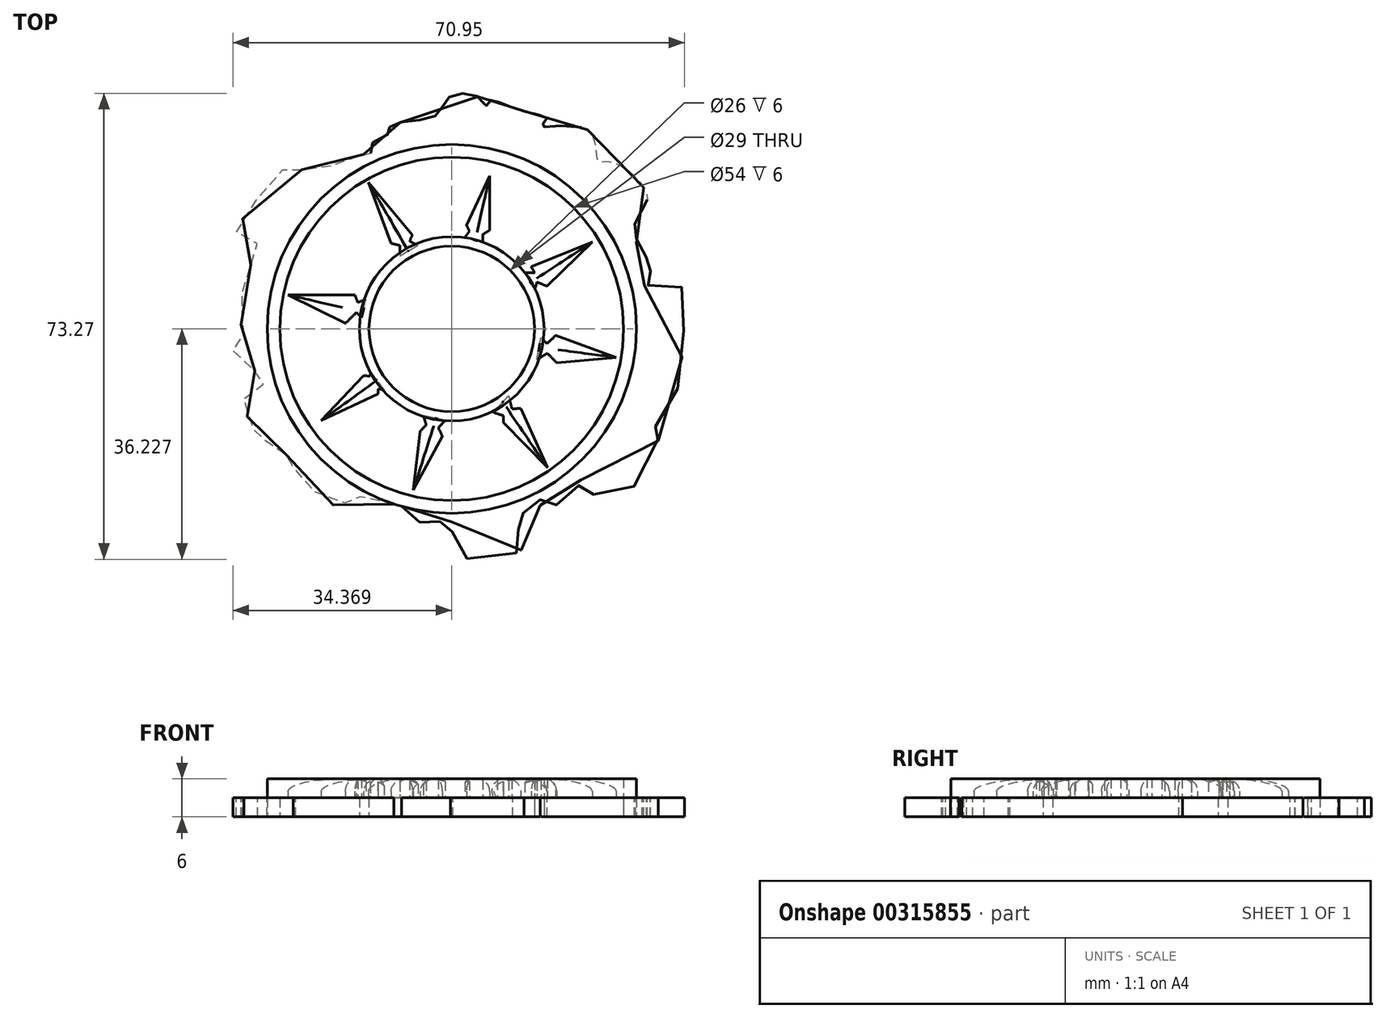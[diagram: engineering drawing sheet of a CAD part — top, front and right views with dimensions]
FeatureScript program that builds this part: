
annotation { "Feature Type Name" : "Feature", "Feature Type Description" : "" }
export const myFeature = defineFeature(function(context is Context, id is Id, definition is map)
    precondition{}
    {
        {
            var Q0;
            Q0=qCreatedBy(makeId("Top.planeOp"),FACE);
            var sketch = newSketch(context, id + "F0", { "sketchPlane" : qUnion([Q0])});
            skCircle(sketch, "E0", {"center": v(-38.6, -30.63) * mm, "radius": 6.5 * mm});
            skCircle(sketch, "E1", {"center": v(-38.6, -30.63) * mm, "radius": 7.25 * mm});
            skCircle(sketch, "E2", {"center": v(-38.6, -30.63) * mm, "radius": 14.5 * mm});
            skCircle(sketch, "E3", {"center": v(-38.6, -30.63) * mm, "radius": 13.5 * mm});
            skCircle(sketch, "E4", {"center": v(-38.6, -30.63) * mm, "radius": 18.94 * mm});
            skSolve(sketch);
        }
        {
            var Q0;
            Q0=makeQuery(id+"F0.imprint","IMPRINT",FACE,{"disambiguationData":[TD([[makeQuery(id+"F0.imprint","IMPRINT",EDGE,{"derivedFrom":sQuery(id+"F0.wireOp",EDGE,"E2")}),-1.0]])]});
            var Q1;
            Q1=makeQuery(id+"F0.imprint","IMPRINT",FACE,{"disambiguationData":[TD([[makeQuery(id+"F0.imprint","IMPRINT",EDGE,{"derivedFrom":sQuery(id+"F0.wireOp",EDGE,"E1")}),-1.0]])]});
            extrude(context, id + "F1", {"entities" : qUnion([Q0, Q1]), "depth" : 1.5 * mm});
        }
        {
            var Q0;
            Q0=makeQuery(id+"F0.imprint","IMPRINT",FACE,{"disambiguationData":[TD([[makeQuery(id+"F0.imprint","IMPRINT",EDGE,{"derivedFrom":sQuery(id+"F0.wireOp",EDGE,"E0")}),1.0]])]});
            extrude(context, id + "F2", {"entities" : qUnion([Q0]), "depth" : 1.5 * mm});
        }
        {
            var Q0;
            Q0=makeQuery(id+"F0.imprint","IMPRINT",FACE,{"disambiguationData":[TD([[makeQuery(id+"F0.imprint","IMPRINT",EDGE,{"derivedFrom":sQuery(id+"F0.wireOp",EDGE,"E0")}),-1.0]])]});
            var Q1;
            Q1=makeQuery(id+"F0.imprint","IMPRINT",FACE,{"disambiguationData":[TD([[makeQuery(id+"F0.imprint","IMPRINT",EDGE,{"derivedFrom":sQuery(id+"F0.wireOp",EDGE,"E2")}),1.0]])]});
            extrude(context, id + "F3", {"entities" : qUnion([Q0, Q1]), "depth" : 3 * mm});
        }
        {
            var Q0;
            Q0=makeQuery(id+"F1.opExtrude","CAP_FACE",FACE,{"disambiguationData":[OSD([sQuery(id+"F0.wireOp",EDGE,"E2"),sQuery(id+"F0.wireOp",EDGE,"E4")])],"isStart":false});
            var sketch = newSketch(context, id + "F4", { "sketchPlane" : qUnion([Q0])});
            skFitSpline(sketch, "E5", {"points": [v(-46.5, -18) * mm, v(-45.94, -16.8) * mm, v(-45.07, -17.04) * mm, v(-44.8, -15.91) * mm, v(-43.72, -15.48) * mm, v(-43.38, -14.66) * mm, v(-39.92, -13.9) * mm, v(-38.76, -12.36) * mm, v(-36.28, -12.56) * mm, v(-35.92, -13.17) * mm, v(-35.64, -12.7) * mm, v(-34.55, -12.95) * mm, v(-31.96, -13.77) * mm, v(-31.1, -14.15) * mm, v(-31.57, -14.7) * mm, v(-27.95, -14.98) * mm, v(-27.15, -17.35) * mm, v(-26, -17.52) * mm, v(-23.25, -20.55) * mm, v(-24.26, -22.27) * mm, v(-23.64, -22.98) * mm, v(-24.16, -23.72) * mm, v(-23.33, -24.67) * mm, v(-23.5, -25.82) * mm, v(-22.98, -26.1) * mm, v(-23.6, -27.16) * mm, v(-21.08, -26.98) * mm, v(-20.36, -29.96) * mm, v(-21.61, -37.2) * mm, v(-23.01, -38.83) * mm, v(-22.4, -39.36) * mm, v(-26.3, -44.26) * mm, v(-28.44, -42.51) * mm, v(-28.92, -43.75) * mm, v(-31.1, -44.35) * mm, v(-31.63, -43.88) * mm, v(-31.87, -45.04) * mm, v(-33.76, -45.11) * mm, v(-32.97, -47.27) * mm, v(-33.6, -48.27) * mm, v(-38.54, -48.12) * mm, v(-38.58, -45.84) * mm, v(-39.53, -45.78) * mm, v(-39.8, -45.55) * mm, v(-41.55, -45.8) * mm, v(-42.55, -44.58) * mm, v(-45.15, -44.23) * mm, v(-46.53, -43.44) * mm, v(-47.2, -44.57) * mm, v(-50.2, -42.7) * mm, v(-51.05, -41.36) * mm, v(-50.92, -40.53) * mm, v(-52.62, -40.53) * mm, v(-53.29, -39.18) * mm, v(-53.89, -38.78) * mm, v(-54.44, -38.06) * mm, v(-54.8, -35.68) * mm, v(-53.46, -35.02) * mm, v(-53.2, -34.17) * mm, v(-54.88, -33.72) * mm, v(-55.7, -31.95) * mm, v(-54.87, -31.2) * mm, v(-55.08, -30.95) * mm, v(-55.07, -29.3) * mm, v(-55.12, -28.68) * mm, v(-55, -27.6) * mm, v(-54.44, -25.78) * mm, v(-54.02, -24.55) * mm, v(-53.95, -23.78) * mm, v(-55.45, -23.13) * mm, v(-54.16, -20.82) * mm, v(-51.76, -18.11) * mm, v(-50.53, -18.47) * mm, v(-50.04, -17.48) * mm, v(-46.5, -18) * mm]});
            skSolve(sketch);
        }
        {
            var Q0;
            {var subQ0=sQuery(id+"F4.wireOp",EDGE,"E5");var subQ1=makeQuery(id+"F1.opExtrude","CAP_EDGE",EDGE,{"disambiguationData":[OSD([sQuery(id+"F0.wireOp",EDGE,"E4")])],"isStart":false});var subQ2=makeQuery(id+"F4.imprint","INTERSECT",VERTEX,{"disambiguationData":[OD(0.0)],"derivedFrom":[subQ1,subQ0]});Q0=makeQuery(id+"F4.imprint","IMPRINT",FACE,{"disambiguationData":[TD([[makeQuery(id+"F4.imprint","IMPRINT",EDGE,{"disambiguationData":[TD([[subQ2,-1.0]])],"derivedFrom":subQ0}),1.0]])]});}
            var Q1;
            {var subQ0=sQuery(id+"F4.wireOp",EDGE,"E5");var subQ1=makeQuery(id+"F1.opExtrude","CAP_EDGE",EDGE,{"disambiguationData":[OSD([sQuery(id+"F0.wireOp",EDGE,"E4")])],"isStart":false});var subQ2=makeQuery(id+"F4.imprint","INTERSECT",VERTEX,{"disambiguationData":[OD(0.0)],"derivedFrom":[subQ1,subQ0]});Q1=makeQuery(id+"F4.imprint","IMPRINT",FACE,{"disambiguationData":[TD([[makeQuery(id+"F4.imprint","IMPRINT",EDGE,{"disambiguationData":[TD([[subQ2,1.0]])],"derivedFrom":subQ0}),1.0]])]});}
            extrude(context, id + "F5", {"entities" : qUnion([Q0, Q1]), "operationType" : NewBodyOperationType.REMOVE, "oppositeDirection" : true, "depth" : 1.5 * mm});
        }
        {
            var Q0;
            {var subQ0=sQuery(id+"F4.wireOp",EDGE,"E5");var subQ1=makeQuery(id+"F1.opExtrude","CAP_EDGE",EDGE,{"disambiguationData":[OSD([sQuery(id+"F0.wireOp",EDGE,"E2")])],"isStart":false});var subQ2=makeQuery(id+"F4.imprint","INTERSECT",VERTEX,{"disambiguationData":[OD(0.0)],"derivedFrom":[subQ1,subQ0]});Q0=makeQuery(id+"F4.imprint","IMPRINT",FACE,{"disambiguationData":[TD([[makeQuery(id+"F4.imprint","IMPRINT",EDGE,{"disambiguationData":[TD([[subQ2,-1.0]])],"derivedFrom":subQ0}),-1.0]])]});}
            var sketch = newSketch(context, id + "F6", { "sketchPlane" : qUnion([Q0])});
            skLineSegment(sketch, "E6", {"start": v(-37.57, -23.46) * mm, "end": v(-37.22, -22.96) * mm});
            skLineSegment(sketch, "E7", {"start": v(-37.22, -22.96) * mm, "end": v(-37.45, -22.46) * mm});
            skLineSegment(sketch, "E8", {"start": v(-37.45, -22.46) * mm, "end": v(-35.62, -18.6) * mm});
            skLineSegment(sketch, "E9", {"start": v(-35.62, -18.6) * mm, "end": v(-35.62, -22.88) * mm});
            skLineSegment(sketch, "E10", {"start": v(-35.62, -22.88) * mm, "end": v(-36.17, -23.2) * mm});
            skLineSegment(sketch, "E11", {"start": v(-36.17, -23.2) * mm, "end": v(-36.17, -23.8) * mm});
            skLineSegment(sketch, "E12", {"start": v(-36.17, -23.8) * mm, "end": v(-37.57, -23.46) * mm});
            skLineSegment(sketch, "E13", {"start": v(-36.87, -23.63) * mm, "end": v(-35.62, -18.6) * mm});
            skLineSegment(sketch, "E14", {"start": v(-35.62, -22.88) * mm, "end": v(-35.9, -23.04) * mm});
            skLineSegment(sketch, "E15", {"start": v(-32.86, -26.23) * mm, "end": v(-32.07, -26.23) * mm});
            skLineSegment(sketch, "E16", {"start": v(-32.07, -26.23) * mm, "end": v(-32.36, -25.76) * mm});
            skLineSegment(sketch, "E17", {"start": v(-32.36, -25.76) * mm, "end": v(-27.56, -23.8) * mm});
            skLineSegment(sketch, "E18", {"start": v(-27.56, -23.8) * mm, "end": v(-31.13, -27.27) * mm});
            skLineSegment(sketch, "E19", {"start": v(-31.13, -27.27) * mm, "end": v(-31.91, -26.96) * mm});
            skLineSegment(sketch, "E20", {"start": v(-31.91, -26.96) * mm, "end": v(-32.07, -27.52) * mm});
            skLineSegment(sketch, "E21", {"start": v(-32.07, -27.52) * mm, "end": v(-32.86, -26.23) * mm});
            skLineSegment(sketch, "E22", {"start": v(-32.47, -26.88) * mm, "end": v(-27.56, -23.8) * mm});
            skLineSegment(sketch, "E23", {"start": v(-31.6, -31.31) * mm, "end": v(-31.12, -31.8) * mm});
            skLineSegment(sketch, "E24", {"start": v(-31.12, -31.8) * mm, "end": v(-30.44, -31.14) * mm});
            skLineSegment(sketch, "E25", {"start": v(-30.44, -31.14) * mm, "end": v(-25.68, -32.88) * mm});
            skLineSegment(sketch, "E26", {"start": v(-25.68, -32.88) * mm, "end": v(-30.36, -33.3) * mm});
            skLineSegment(sketch, "E27", {"start": v(-30.36, -33.3) * mm, "end": v(-31.09, -32.55) * mm});
            skLineSegment(sketch, "E28", {"start": v(-31.09, -32.55) * mm, "end": v(-31.91, -33.05) * mm});
            skLineSegment(sketch, "E29", {"start": v(-31.91, -33.05) * mm, "end": v(-31.6, -31.31) * mm});
            skLineSegment(sketch, "E30", {"start": v(-31.75, -32.18) * mm, "end": v(-25.68, -32.88) * mm});
            skLineSegment(sketch, "E31", {"start": v(-33.19, -36.87) * mm, "end": v(-31.09, -41.53) * mm});
            skLineSegment(sketch, "E32", {"start": v(-31.09, -41.53) * mm, "end": v(-34.53, -38) * mm});
            skLineSegment(sketch, "E33", {"start": v(-35, -36.82) * mm, "end": v(-34.13, -35.89) * mm});
            skLineSegment(sketch, "E34", {"start": v(-34.13, -35.89) * mm, "end": v(-33.87, -36.93) * mm});
            skLineSegment(sketch, "E35", {"start": v(-33.87, -36.93) * mm, "end": v(-33.19, -36.87) * mm});
            skLineSegment(sketch, "E36", {"start": v(-40.83, -37.47) * mm, "end": v(-40.6, -38.17) * mm});
            skLineSegment(sketch, "E37", {"start": v(-40.6, -38.17) * mm, "end": v(-41.07, -38.68) * mm});
            skLineSegment(sketch, "E38", {"start": v(-41.07, -38.68) * mm, "end": v(-41.62, -43.3) * mm});
            skLineSegment(sketch, "E39", {"start": v(-41.62, -43.3) * mm, "end": v(-39.33, -39.09) * mm});
            skLineSegment(sketch, "E40", {"start": v(-39.33, -39.09) * mm, "end": v(-39.66, -38.4) * mm});
            skLineSegment(sketch, "E41", {"start": v(-39.66, -38.4) * mm, "end": v(-39.11, -37.83) * mm});
            skLineSegment(sketch, "E42", {"start": v(-39.11, -37.83) * mm, "end": v(-40.83, -37.47) * mm});
            skLineSegment(sketch, "E43", {"start": v(-39.97, -37.65) * mm, "end": v(-41.62, -43.3) * mm});
            skLineSegment(sketch, "E44", {"start": v(-44.97, -34) * mm, "end": v(-45.02, -34.36) * mm});
            skLineSegment(sketch, "E45", {"start": v(-45.02, -34.36) * mm, "end": v(-45.53, -34.3) * mm});
            skLineSegment(sketch, "E46", {"start": v(-45.53, -34.3) * mm, "end": v(-48.85, -37.83) * mm});
            skLineSegment(sketch, "E47", {"start": v(-48.85, -37.83) * mm, "end": v(-44.4, -35.75) * mm});
            skLineSegment(sketch, "E48", {"start": v(-44.4, -35.75) * mm, "end": v(-44.4, -35.35) * mm});
            skLineSegment(sketch, "E49", {"start": v(-44.4, -35.35) * mm, "end": v(-43.92, -35.4) * mm});
            skLineSegment(sketch, "E50", {"start": v(-43.92, -35.4) * mm, "end": v(-44.97, -34) * mm});
            skLineSegment(sketch, "E51", {"start": v(-44.44, -34.7) * mm, "end": v(-48.85, -37.83) * mm});
            skLineSegment(sketch, "E52", {"start": v(-45.35, -28.32) * mm, "end": v(-45.99, -28.56) * mm});
            skLineSegment(sketch, "E53", {"start": v(-45.99, -28.56) * mm, "end": v(-46.21, -27.96) * mm});
            skLineSegment(sketch, "E54", {"start": v(-46.21, -27.96) * mm, "end": v(-51.45, -27.96) * mm});
            skLineSegment(sketch, "E55", {"start": v(-51.45, -27.96) * mm, "end": v(-46.95, -30.2) * mm});
            skLineSegment(sketch, "E56", {"start": v(-46.95, -30.2) * mm, "end": v(-46.09, -29.33) * mm});
            skLineSegment(sketch, "E57", {"start": v(-46.09, -29.33) * mm, "end": v(-45.68, -29.74) * mm});
            skLineSegment(sketch, "E58", {"start": v(-45.68, -29.74) * mm, "end": v(-45.35, -28.32) * mm});
            skLineSegment(sketch, "E59", {"start": v(-45.52, -29.03) * mm, "end": v(-51.45, -27.96) * mm});
            skLineSegment(sketch, "E60", {"start": v(-41.26, -24.07) * mm, "end": v(-41.91, -23.74) * mm});
            skLineSegment(sketch, "E61", {"start": v(-41.91, -23.74) * mm, "end": v(-41.7, -23.25) * mm});
            skLineSegment(sketch, "E62", {"start": v(-41.7, -23.25) * mm, "end": v(-45.13, -19.12) * mm});
            skLineSegment(sketch, "E63", {"start": v(-45.13, -19.12) * mm, "end": v(-43.36, -23.9) * mm});
            skLineSegment(sketch, "E64", {"start": v(-43.36, -23.9) * mm, "end": v(-42.68, -24.07) * mm});
            skLineSegment(sketch, "E65", {"start": v(-42.68, -24.07) * mm, "end": v(-42.68, -24.9) * mm});
            skLineSegment(sketch, "E66", {"start": v(-42.68, -24.9) * mm, "end": v(-41.26, -24.07) * mm});
            skLineSegment(sketch, "E67", {"start": v(-41.97, -24.48) * mm, "end": v(-45.13, -19.12) * mm});
            skLineSegment(sketch, "E68", {"start": v(-34.53, -38) * mm, "end": v(-34.53, -37.45) * mm});
            skLineSegment(sketch, "E69", {"start": v(-34.53, -37.45) * mm, "end": v(-35.54, -37.13) * mm});
            skLineSegment(sketch, "E70", {"start": v(-35.54, -37.13) * mm, "end": v(-35, -36.82) * mm});
            skLineSegment(sketch, "E71", {"start": v(-31.09, -41.53) * mm, "end": v(-34.72, -36.52) * mm});
            skSolve(sketch);
        }
        {
            var Q0;
            Q0=makeQuery(id+"F6.imprint","IMPRINT",FACE,{"disambiguationData":[TD([[makeQuery(id+"F6.imprint","IMPRINT",EDGE,{"derivedFrom":sQuery(id+"F6.wireOp",EDGE,"E9")}),-1.0]])]});
            var Q1;
            {var subQ1=sQuery(id+"F6.wireOp",EDGE,"E6");Q1=makeQuery(id+"F6.imprint","IMPRINT",FACE,{"disambiguationData":[TD([[makeQuery(id+"F6.imprint","IMPRINT",EDGE,{"derivedFrom":subQ1}),-1.0]])]});}
            extrude(context, id + "F7", {"entities" : qUnion([Q0, Q1]), "depth" : 1.5 * mm});
        }
        {
            var Q0;
            Q0=makeQuery(id+"F7.opExtrude","CAP_EDGE",EDGE,{"disambiguationData":[OSD([sQuery(id+"F6.wireOp",EDGE,"E9")])],"isStart":false});
            var Q1;
            Q1=makeQuery(id+"F7.opExtrude","CAP_EDGE",EDGE,{"disambiguationData":[OSD([sQuery(id+"F6.wireOp",EDGE,"E8")])],"isStart":false});
            fillet(context, id + "F8", {"entities" : qUnion([Q0, Q1]), "radius" : 1 * mm, "tangentPropagation" : true, "allowEdgeOverflow" : false});
        }
        {
            var Q0;
            Q0 = qSketchRegion(id + "F6", true);
            extrude(context, id + "F9", {"entities" : qUnion([Q0]), "depth" : 1.5 * mm});
        }
        {
            var Q0;
            Q0=makeQuery(id+"F9.opExtrude","CAP_EDGE",EDGE,{"disambiguationData":[OSD([sQuery(id+"F6.wireOp",EDGE,"E62")])],"isStart":false});
            var Q1;
            Q1=makeQuery(id+"F9.opExtrude","CAP_EDGE",EDGE,{"disambiguationData":[OSD([sQuery(id+"F6.wireOp",EDGE,"E63")])],"isStart":false});
            var Q2;
            Q2=makeQuery(id+"F9.opExtrude","CAP_EDGE",EDGE,{"disambiguationData":[OSD([sQuery(id+"F6.wireOp",EDGE,"E9")])],"isStart":false});
            var Q3;
            Q3=makeQuery(id+"F9.opExtrude","CAP_EDGE",EDGE,{"disambiguationData":[OSD([sQuery(id+"F6.wireOp",EDGE,"E8")])],"isStart":false});
            var Q4;
            Q4=makeQuery(id+"F9.opExtrude","CAP_EDGE",EDGE,{"disambiguationData":[OSD([sQuery(id+"F6.wireOp",EDGE,"E17")])],"isStart":false});
            var Q5;
            Q5=makeQuery(id+"F9.opExtrude","CAP_EDGE",EDGE,{"disambiguationData":[OSD([sQuery(id+"F6.wireOp",EDGE,"E18")])],"isStart":false});
            var Q6;
            Q6=makeQuery(id+"F9.opExtrude","CAP_EDGE",EDGE,{"disambiguationData":[OSD([sQuery(id+"F6.wireOp",EDGE,"E54")])],"isStart":false});
            var Q7;
            Q7=makeQuery(id+"F9.opExtrude","CAP_EDGE",EDGE,{"disambiguationData":[OSD([sQuery(id+"F6.wireOp",EDGE,"E55")])],"isStart":false});
            var Q8;
            Q8=makeQuery(id+"F9.opExtrude","CAP_EDGE",EDGE,{"disambiguationData":[OSD([sQuery(id+"F6.wireOp",EDGE,"E46")])],"isStart":false});
            var Q9;
            Q9=makeQuery(id+"F9.opExtrude","CAP_EDGE",EDGE,{"disambiguationData":[OSD([sQuery(id+"F6.wireOp",EDGE,"E47")])],"isStart":false});
            var Q10;
            Q10=makeQuery(id+"F9.opExtrude","CAP_EDGE",EDGE,{"disambiguationData":[OSD([sQuery(id+"F6.wireOp",EDGE,"E38")])],"isStart":false});
            var Q11;
            Q11=makeQuery(id+"F9.opExtrude","CAP_EDGE",EDGE,{"disambiguationData":[OSD([sQuery(id+"F6.wireOp",EDGE,"E39")])],"isStart":false});
            var Q12;
            Q12=makeQuery(id+"F9.opExtrude","CAP_EDGE",EDGE,{"disambiguationData":[OSD([sQuery(id+"F6.wireOp",EDGE,"E32")])],"isStart":false});
            var Q13;
            Q13=makeQuery(id+"F9.opExtrude","CAP_EDGE",EDGE,{"disambiguationData":[OSD([sQuery(id+"F6.wireOp",EDGE,"E31")])],"isStart":false});
            var Q14;
            Q14=makeQuery(id+"F9.opExtrude","CAP_EDGE",EDGE,{"disambiguationData":[OSD([sQuery(id+"F6.wireOp",EDGE,"E26")])],"isStart":false});
            var Q15;
            Q15=makeQuery(id+"F9.opExtrude","CAP_EDGE",EDGE,{"disambiguationData":[OSD([sQuery(id+"F6.wireOp",EDGE,"E25")])],"isStart":false});
            fillet(context, id + "F10", {"entities" : qUnion([Q0, Q1, Q2, Q3, Q4, Q5, Q6, Q7, Q8, Q9, Q10, Q11, Q12, Q13, Q14, Q15]), "radius" : 1 * mm, "tangentPropagation" : true, "allowEdgeOverflow" : false});
        }
        {
            var Q0;
            Q0=makeQuery(id+"F9.opExtrude","SWEPT_BODY",BODY,{"disambiguationData":[OSD([sQuery(id+"F6.wireOp",EDGE,"E60"),sQuery(id+"F6.wireOp",EDGE,"E61"),sQuery(id+"F6.wireOp",EDGE,"E62"),sQuery(id+"F6.wireOp",EDGE,"E63"),sQuery(id+"F6.wireOp",EDGE,"E64"),sQuery(id+"F6.wireOp",EDGE,"E65"),sQuery(id+"F6.wireOp",EDGE,"E66")])]});
            var Q1;
            Q1=makeQuery(id+"F9.opExtrude","SWEPT_BODY",BODY,{"disambiguationData":[OSD([sQuery(id+"F6.wireOp",EDGE,"E52"),sQuery(id+"F6.wireOp",EDGE,"E53"),sQuery(id+"F6.wireOp",EDGE,"E54"),sQuery(id+"F6.wireOp",EDGE,"E55"),sQuery(id+"F6.wireOp",EDGE,"E56"),sQuery(id+"F6.wireOp",EDGE,"E57"),sQuery(id+"F6.wireOp",EDGE,"E58")])]});
            var Q2;
            Q2=makeQuery(id+"F9.opExtrude","SWEPT_BODY",BODY,{"disambiguationData":[OSD([sQuery(id+"F6.wireOp",EDGE,"E36"),sQuery(id+"F6.wireOp",EDGE,"E37"),sQuery(id+"F6.wireOp",EDGE,"E38"),sQuery(id+"F6.wireOp",EDGE,"E39"),sQuery(id+"F6.wireOp",EDGE,"E40"),sQuery(id+"F6.wireOp",EDGE,"E41"),sQuery(id+"F6.wireOp",EDGE,"E42")])]});
            var Q3;
            Q3=makeQuery(id+"F9.opExtrude","SWEPT_BODY",BODY,{"disambiguationData":[OSD([sQuery(id+"F6.wireOp",EDGE,"E44"),sQuery(id+"F6.wireOp",EDGE,"E45"),sQuery(id+"F6.wireOp",EDGE,"E46"),sQuery(id+"F6.wireOp",EDGE,"E47"),sQuery(id+"F6.wireOp",EDGE,"E48"),sQuery(id+"F6.wireOp",EDGE,"E49"),sQuery(id+"F6.wireOp",EDGE,"E50")])]});
            var Q4;
            Q4=makeQuery(id+"F9.opExtrude","SWEPT_BODY",BODY,{"disambiguationData":[OSD([sQuery(id+"F6.wireOp",EDGE,"E15"),sQuery(id+"F6.wireOp",EDGE,"E16"),sQuery(id+"F6.wireOp",EDGE,"E17"),sQuery(id+"F6.wireOp",EDGE,"E18"),sQuery(id+"F6.wireOp",EDGE,"E19"),sQuery(id+"F6.wireOp",EDGE,"E20"),sQuery(id+"F6.wireOp",EDGE,"E21")])]});
            var Q5;
            Q5=makeQuery(id+"F9.opExtrude","SWEPT_BODY",BODY,{"disambiguationData":[OSD([sQuery(id+"F6.wireOp",EDGE,"E6"),sQuery(id+"F6.wireOp",EDGE,"E7"),sQuery(id+"F6.wireOp",EDGE,"E8"),sQuery(id+"F6.wireOp",EDGE,"E9"),sQuery(id+"F6.wireOp",EDGE,"E10"),sQuery(id+"F6.wireOp",EDGE,"E11"),sQuery(id+"F6.wireOp",EDGE,"E12"),sQuery(id+"F6.wireOp",EDGE,"E14")])]});
            var Q6;
            Q6=makeQuery(id+"F2.opExtrude","SWEPT_BODY",BODY,{"disambiguationData":[OSD([sQuery(id+"F0.wireOp",EDGE,"E0")])]});
            var Q7;
            Q7=makeQuery(id+"F3.opExtrude","SWEPT_BODY",BODY,{"disambiguationData":[OSD([sQuery(id+"F0.wireOp",EDGE,"E2"),sQuery(id+"F0.wireOp",EDGE,"E3")])]});
            var Q8;
            Q8=makeQuery(id+"F9.opExtrude","SWEPT_BODY",BODY,{"disambiguationData":[OSD([sQuery(id+"F6.wireOp",EDGE,"E23"),sQuery(id+"F6.wireOp",EDGE,"E24"),sQuery(id+"F6.wireOp",EDGE,"E25"),sQuery(id+"F6.wireOp",EDGE,"E26"),sQuery(id+"F6.wireOp",EDGE,"E27"),sQuery(id+"F6.wireOp",EDGE,"E28"),sQuery(id+"F6.wireOp",EDGE,"E29")])]});
            var Q9;
            Q9=makeQuery(id+"F1.opExtrude","SWEPT_BODY",BODY,{"disambiguationData":[OSD([sQuery(id+"F0.wireOp",EDGE,"E1"),sQuery(id+"F0.wireOp",EDGE,"E3")])]});
            var Q10;
            Q10=makeQuery(id+"F1.opExtrude","SWEPT_BODY",BODY,{"disambiguationData":[OSD([sQuery(id+"F0.wireOp",EDGE,"E2"),sQuery(id+"F0.wireOp",EDGE,"E4")])]});
            var Q11;
            Q11=makeQuery(id+"F3.opExtrude","SWEPT_BODY",BODY,{"disambiguationData":[OSD([sQuery(id+"F0.wireOp",EDGE,"E0"),sQuery(id+"F0.wireOp",EDGE,"E1")])]});
            var Q12;
            Q12=makeQuery(id+"F9.opExtrude","SWEPT_BODY",BODY,{"disambiguationData":[OSD([sQuery(id+"F6.wireOp",EDGE,"E31"),sQuery(id+"F6.wireOp",EDGE,"E32"),sQuery(id+"F6.wireOp",EDGE,"E33"),sQuery(id+"F6.wireOp",EDGE,"E34"),sQuery(id+"F6.wireOp",EDGE,"E35"),sQuery(id+"F6.wireOp",EDGE,"E68"),sQuery(id+"F6.wireOp",EDGE,"E69"),sQuery(id+"F6.wireOp",EDGE,"E70")])]});
            var Q13;
            Q13=makeQuery(id+"F7.opExtrude","SWEPT_BODY",BODY,{"disambiguationData":[OSD([sQuery(id+"F6.wireOp",EDGE,"E6"),sQuery(id+"F6.wireOp",EDGE,"E7"),sQuery(id+"F6.wireOp",EDGE,"E8"),sQuery(id+"F6.wireOp",EDGE,"E9"),sQuery(id+"F6.wireOp",EDGE,"E10"),sQuery(id+"F6.wireOp",EDGE,"E11"),sQuery(id+"F6.wireOp",EDGE,"E12"),sQuery(id+"F6.wireOp",EDGE,"E14")])]});
            var Q14;
            Q14=sQuery(id+"F0.wireOp",VERTEX,"E3.center");
            transform(context, id + "F11", {"entities" : qUnion([Q0, Q1, Q2, Q3, Q4, Q5, Q6, Q7, Q8, Q9, Q10, Q11, Q12, Q13]), "transformType" : TransformType.SCALE_UNIFORMLY, "scale" : 2, "scalePoint" : qUnion([Q14]), "makeCopy" : false});
        }
    });
